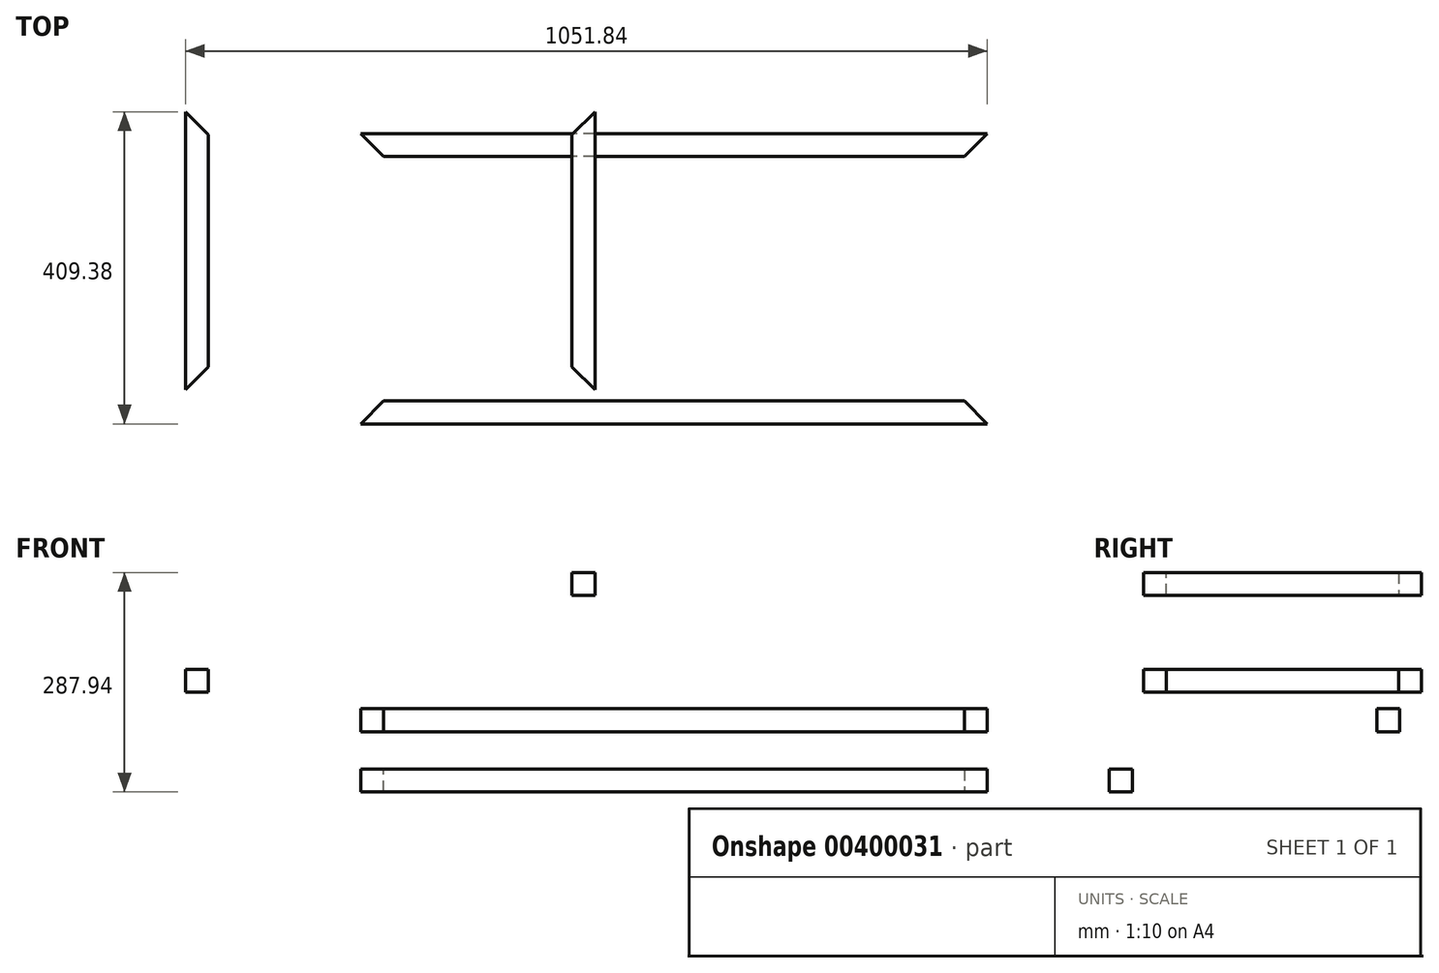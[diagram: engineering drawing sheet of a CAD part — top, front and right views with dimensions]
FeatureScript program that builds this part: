
annotation { "Feature Type Name" : "Feature", "Feature Type Description" : "" }
export const myFeature = defineFeature(function(context is Context, id is Id, definition is map)
    precondition{}
    {
        {
            var Q0;
            Q0=qCreatedBy(makeId("Right.planeOp"),FACE);
            var sketch = newSketch(context, id + "F0", { "sketchPlane" : qUnion([Q0])});
            skLineSegment(sketch, "E0.bottom", {"start": v(-358.38, -183.1) * mm, "end": v(-1120.38, -183.1) * mm});
            skLineSegment(sketch, "E0.top", {"start": v(-358.38, 121.7) * mm, "end": v(-1120.38, 121.7) * mm});
            skLineSegment(sketch, "E0.left", {"start": v(-358.38, -183.1) * mm, "end": v(-358.38, 121.7) * mm});
            skLineSegment(sketch, "E0.right", {"start": v(-1120.38, -183.1) * mm, "end": v(-1120.38, 121.7) * mm});
            skPoint(sketch, "E0.middle", {"position": v(-739.38, -30.7) * mm});
            skLineSegment(sketch, "E1.bottom", {"start": v(-58.33, -285.78) * mm, "end": v(-28.33, -285.78) * mm});
            skLineSegment(sketch, "E1.top", {"start": v(-58.33, -255.78) * mm, "end": v(-28.33, -255.78) * mm});
            skLineSegment(sketch, "E1.left", {"start": v(-58.33, -285.78) * mm, "end": v(-58.33, -255.78) * mm});
            skLineSegment(sketch, "E1.right", {"start": v(-28.33, -285.78) * mm, "end": v(-28.33, -255.78) * mm});
            skPoint(sketch, "E1.middle", {"position": v(-43.33, -270.78) * mm});
            skLineSegment(sketch, "E2.bottom", {"start": v(32.98, -32.36) * mm, "end": v(-729.02, -32.36) * mm});
            skLineSegment(sketch, "E2.top", {"start": v(32.98, 272.44) * mm, "end": v(-729.02, 272.44) * mm});
            skLineSegment(sketch, "E2.left", {"start": v(32.98, -32.36) * mm, "end": v(32.98, 272.44) * mm});
            skLineSegment(sketch, "E2.right", {"start": v(-729.02, -32.36) * mm, "end": v(-729.02, 272.44) * mm});
            skPoint(sketch, "E2.middle", {"position": v(-348.02, 120.04) * mm});
            skLineSegment(sketch, "E3.bottom", {"start": v(333.02, -135.04) * mm, "end": v(363.02, -135.04) * mm});
            skLineSegment(sketch, "E3.top", {"start": v(333.02, -105.04) * mm, "end": v(363.02, -105.04) * mm});
            skLineSegment(sketch, "E3.left", {"start": v(333.02, -135.04) * mm, "end": v(333.02, -105.04) * mm});
            skLineSegment(sketch, "E3.right", {"start": v(363.02, -135.04) * mm, "end": v(363.02, -105.04) * mm});
            skPoint(sketch, "E3.middle", {"position": v(348.02, -120.04) * mm});
            skSolve(sketch);
        }
        {
            var Q0;
            Q0=makeQuery(id+"F0.imprint","IMPRINT",FACE,{"disambiguationData":[TD([[makeQuery(id+"F0.imprint","IMPRINT",EDGE,{"derivedFrom":sQuery(id+"F0.wireOp",EDGE,"E1.bottom")}),1.0]])]});
            extrude(context, id + "F1", {"entities" : qUnion([Q0]), "depth" : 762 * mm + 60 * mm});
        }
        {
            var Q0;
            Q0=qCreatedBy(makeId("Front.planeOp"),FACE);
            var sketch = newSketch(context, id + "F2", { "sketchPlane" : qUnion([Q0])});
            skLineSegment(sketch, "E4.bottom", {"start": v(-229.84, -234.01) * mm, "end": v(-199.84, -234.01) * mm});
            skLineSegment(sketch, "E4.top", {"start": v(-229.84, -204.01) * mm, "end": v(-199.84, -204.01) * mm});
            skLineSegment(sketch, "E4.left", {"start": v(-229.84, -234.01) * mm, "end": v(-229.84, -204.01) * mm});
            skLineSegment(sketch, "E4.right", {"start": v(-199.84, -234.01) * mm, "end": v(-199.84, -204.01) * mm});
            skPoint(sketch, "E4.middle", {"position": v(-214.84, -219.01) * mm});
            skSolve(sketch);
        }
        {
            var Q0;
            Q0=makeQuery(id+"F2.imprint","IMPRINT",FACE,{"disambiguationData":[TD([[makeQuery(id+"F2.imprint","IMPRINT",EDGE,{"derivedFrom":sQuery(id+"F2.wireOp",EDGE,"E4.bottom")}),1.0]])]});
            extrude(context, id + "F3", {"entities" : qUnion([Q0]), "depth" : 304.8 * mm + 60 * mm});
        }
        {
            var Q0;
            Q0=qCreatedBy(makeId("Right.planeOp"),FACE);
            var sketch = newSketch(context, id + "F4", { "sketchPlane" : qUnion([Q0])});
            skLineSegment(sketch, "E5.bottom", {"start": v(-379.38, -364.81) * mm, "end": v(-409.38, -364.81) * mm});
            skLineSegment(sketch, "E5.top", {"start": v(-379.38, -334.81) * mm, "end": v(-409.38, -334.81) * mm});
            skLineSegment(sketch, "E5.left", {"start": v(-379.38, -364.81) * mm, "end": v(-379.38, -334.81) * mm});
            skLineSegment(sketch, "E5.right", {"start": v(-409.38, -364.81) * mm, "end": v(-409.38, -334.81) * mm});
            skPoint(sketch, "E5.middle", {"position": v(-394.38, -349.81) * mm});
            skSolve(sketch);
        }
        {
            var Q0;
            Q0=makeQuery(id+"F4.imprint","IMPRINT",FACE,{"disambiguationData":[TD([[makeQuery(id+"F4.imprint","IMPRINT",EDGE,{"derivedFrom":sQuery(id+"F4.wireOp",EDGE,"E5.bottom")}),-1.0]])]});
            extrude(context, id + "F5", {"entities" : qUnion([Q0]), "depth" : 762 * mm + 60 * mm});
        }
        {
            var Q0;
            Q0=qCreatedBy(makeId("Front.planeOp"),FACE);
            var sketch = newSketch(context, id + "F6", { "sketchPlane" : qUnion([Q0])});
            skLineSegment(sketch, "E6.bottom", {"start": v(277.1, -106.87) * mm, "end": v(307.1, -106.87) * mm});
            skLineSegment(sketch, "E6.top", {"start": v(277.1, -76.87) * mm, "end": v(307.1, -76.87) * mm});
            skLineSegment(sketch, "E6.left", {"start": v(277.1, -106.87) * mm, "end": v(277.1, -76.87) * mm});
            skLineSegment(sketch, "E6.right", {"start": v(307.1, -106.87) * mm, "end": v(307.1, -76.87) * mm});
            skPoint(sketch, "E6.middle", {"position": v(292.1, -91.87) * mm});
            skSolve(sketch);
        }
        {
            var Q0;
            Q0=makeQuery(id+"F6.imprint","IMPRINT",FACE,{"disambiguationData":[TD([[makeQuery(id+"F6.imprint","IMPRINT",EDGE,{"derivedFrom":sQuery(id+"F6.wireOp",EDGE,"E6.bottom")}),1.0]])]});
            extrude(context, id + "F7", {"entities" : qUnion([Q0]), "depth" : 304.8 * mm + 60 * mm});
        }
        {
            var Q0;
            Q0=makeQuery(id+"F7.opExtrude","CAP_EDGE",EDGE,{"disambiguationData":[OSD([sQuery(id+"F6.wireOp",EDGE,"E6.left")])],"isStart":true});
            var Q1;
            Q1=makeQuery(id+"F7.opExtrude","CAP_EDGE",EDGE,{"disambiguationData":[OSD([sQuery(id+"F6.wireOp",EDGE,"E6.left")])],"isStart":false});
            var Q2;
            Q2=makeQuery(id+"F3.opExtrude","CAP_EDGE",EDGE,{"disambiguationData":[OSD([sQuery(id+"F2.wireOp",EDGE,"E4.right")])],"isStart":true});
            var Q3;
            Q3=makeQuery(id+"F3.opExtrude","CAP_EDGE",EDGE,{"disambiguationData":[OSD([sQuery(id+"F2.wireOp",EDGE,"E4.right")])],"isStart":false});
            var Q4;
            Q4=makeQuery(id+"F5.opExtrude","CAP_EDGE",EDGE,{"disambiguationData":[OSD([sQuery(id+"F4.wireOp",EDGE,"E5.left")])],"isStart":true});
            var Q5;
            Q5=makeQuery(id+"F5.opExtrude","CAP_EDGE",EDGE,{"disambiguationData":[OSD([sQuery(id+"F4.wireOp",EDGE,"E5.left")])],"isStart":false});
            var Q6;
            Q6=makeQuery(id+"F1.opExtrude","CAP_EDGE",EDGE,{"disambiguationData":[OSD([sQuery(id+"F0.wireOp",EDGE,"E1.left")])],"isStart":false});
            var Q7;
            Q7=makeQuery(id+"F1.opExtrude","CAP_EDGE",EDGE,{"disambiguationData":[OSD([sQuery(id+"F0.wireOp",EDGE,"E1.left")])],"isStart":true});
            chamfer(context, id + "F8", {"entities" : qUnion([Q0, Q1, Q2, Q3, Q4, Q5, Q6, Q7]), "width" : 30 * mm, "tangentPropagation" : true});
        }
    });
